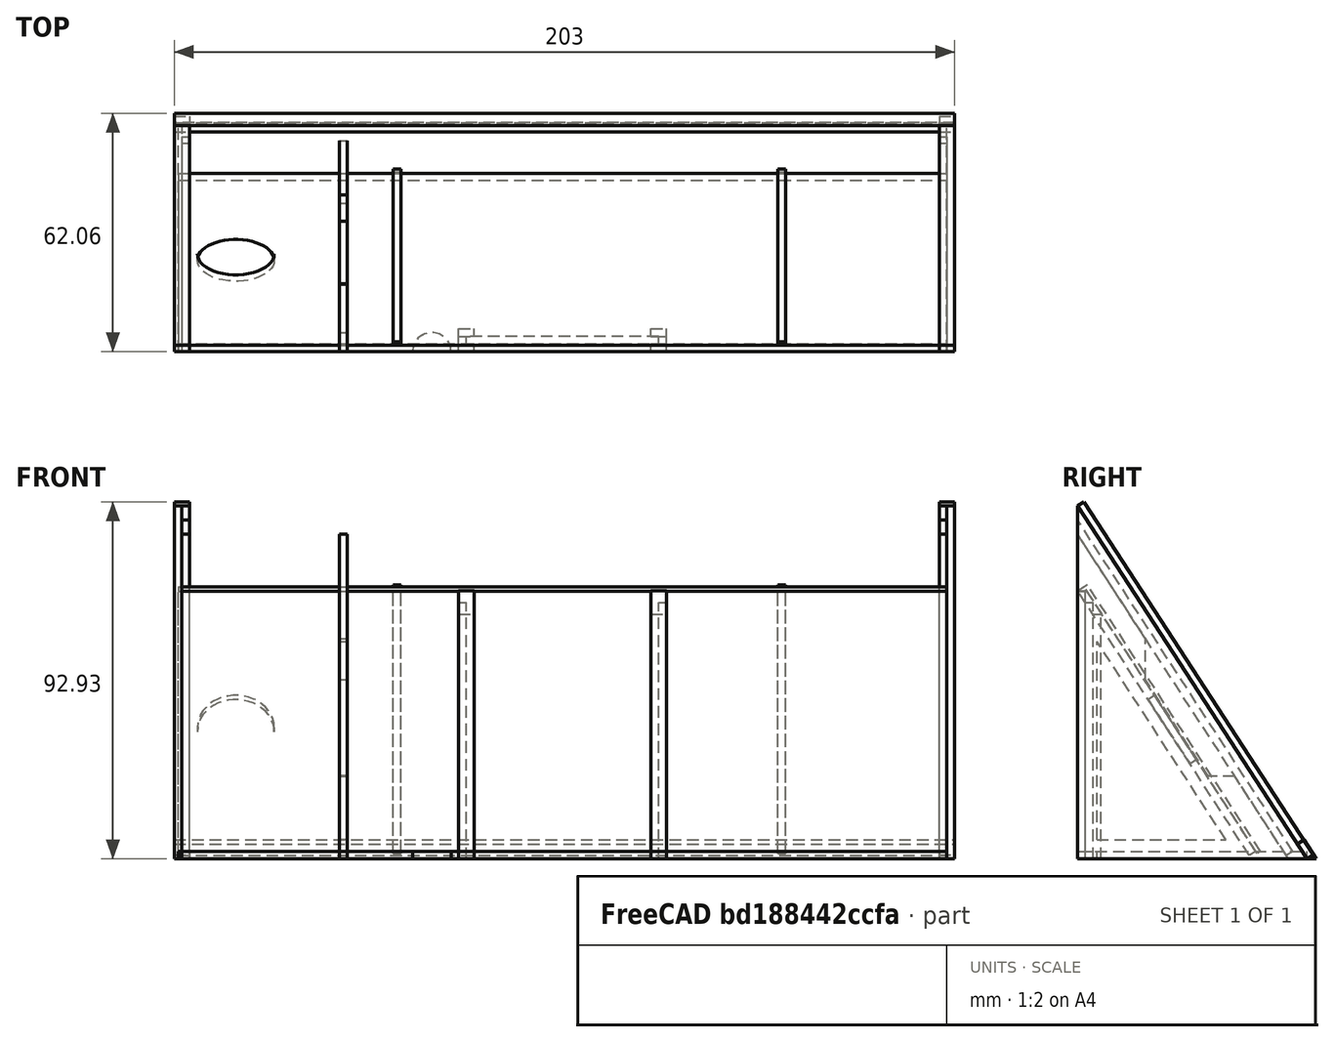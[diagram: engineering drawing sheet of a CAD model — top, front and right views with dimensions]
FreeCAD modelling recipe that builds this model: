
FCSTD DOCUMENT  (FreeCAD 0.16R)
Label: Phone_Stand_Version_1
License: All rights reserved
LicenseURL: http://en.wikipedia.org/wiki/All_rights_reserved
objects: Part::Box×37, Part::Cut×18, Part::Fuse×2, Part::Cylinder×2
note: 59 computed .brp shape members not serialized (recipe doc carries the construction recipe); baked Part::Feature solids carry a one-line shape summary decoded from their .brp

FEATURE [Part::Box] Box  label="Auflage"
  Height = 2
  Length = 200
  Placement = pos=(0,0,0) rot=(1,0,0;2.14676rad)
  Width = 82
FEATURE [Part::Box] Box001  label="Boden"
  Height = 2
  Length = 200
  Placement = pos=(0,-46.35,-2) rot=(0,0,1;0rad)
  Width = 59.65
FEATURE [Part::Box] Box002  label="Rückwand"
  Height = 67.682
  Length = 200
  Placement = pos=(0,-46.338,0) rot=(0,0,1;0rad)
  Width = 2
FEATURE [Part::Box] Box009  label="Cube008"
  Height = 50
  Length = 2
  Placement = pos=(0,13.3,-2) rot=(1,0,0;2.14676rad)
  Width = 110
FEATURE [Part::Box] Box010  label="Cube009"
  Height = 100
  Length = 2
  Placement = pos=(0,-96.35,-3) rot=(0,0,1;0rad)
  Width = 50
FEATURE [Part::Box] Box011  label="Cube010"
  Height = 30
  Length = 10
  Placement = pos=(0,-50,-32) rot=(0,0,1;0rad)
  Width = 70
FEATURE [Part::Cut] Cut002
  Base = -> Box009
  Tool = -> Box011
FEATURE [Part::Cut] Cut003  label="Seitenwand rechts"
  Base = -> Cut002
  Placement = pos=(-1,0,0) rot=(0,0,1;0rad)
  Tool = -> Box010
FEATURE [Part::Box] Box012  label="Cube011"
  Height = 50
  Length = 2
  Placement = pos=(0,13.3,-2) rot=(1,0,0;2.14676rad)
  Width = 110
FEATURE [Part::Box] Box013  label="Cube012"
  Height = 100
  Length = 2
  Placement = pos=(0,-96.35,-3) rot=(0,0,1;0rad)
  Width = 50
FEATURE [Part::Box] Box014  label="Cube013"
  Height = 30
  Length = 10
  Placement = pos=(0,-50,-32) rot=(0,0,1;0rad)
  Width = 70
FEATURE [Part::Cut] Cut004
  Base = -> Box012
  Tool = -> Box014
FEATURE [Part::Cut] Cut005  label="Seitenwand links"
  Base = -> Cut004
  Placement = pos=(200,0,0) rot=(0,0,1;0rad)
  Tool = -> Box013
FEATURE [Part::Box] Box016  label="Cube015"
  Height = 2
  Length = 2
  Placement = pos=(0,9.6,0) rot=(1,0,0;2.14676rad)
  Width = 110
FEATURE [Part::Box] Box017  label="Cube016"
  Height = 20
  Length = 10
  Placement = pos=(0,-56.35,80) rot=(0,0,1;0rad)
  Width = 10
FEATURE [Part::Cut] Cut  label="Führungsleiste links"
  Base = -> Box016
  Placement = pos=(198,0,0) rot=(0,0,1;0rad)
  Tool = -> Box017
FEATURE [Part::Box] Box019  label="Cube018"
  Height = 100
  Length = 2
  Placement = pos=(0,-96.35,-3) rot=(0,0,1;0rad)
  Width = 50
FEATURE [Part::Box] Box028  label="Cube026"
  Height = 15
  Length = 2
  Placement = pos=(-40,13.3,-2) rot=(1,0,0;2.14676rad)
  Width = 110
FEATURE [Part::Box] Box029  label="Cube027"
  Height = 10
  Length = 2
  Placement = pos=(-40,-4,25) rot=(1,0,0;2.14676rad)
  Width = 30
FEATURE [Part::Box] Box030  label="Cube028"
  Height = 70
  Length = 2
  Placement = pos=(-40,-46.35,-2) rot=(0,0,1;0rad)
  Width = 5
FEATURE [Part::Box] Box031  label="Cube029"
  Height = 5
  Length = 2
  Placement = pos=(-40,-46.35,-2) rot=(0,0,1;0rad)
  Width = 50
FEATURE [Part::Box] Box032  label="Cube030"
  Height = 95
  Length = 2
  Placement = pos=(-40,-61.35,-2) rot=(0,0,1;0rad)
  Width = 15
FEATURE [Part::Box] Box033  label="Cube031"
  Height = 10
  Length = 2
  Placement = pos=(-40,-46.35,-12) rot=(0,0,1;0rad)
  Width = 65
FEATURE [Part::Cut] Cut013
  Base = -> Box028
  Tool = -> Box032
FEATURE [Part::Cut] Cut014
  Base = -> Cut013
  Tool = -> Box033
FEATURE [Part::Cut] Cut015  label="Seitenwand rechts001"
  Base = -> Cut003
  Tool = -> Box019
FEATURE [Part::Cut] Cut016
  Base = -> Cut014
  Tool = -> Box029
FEATURE [Part::Fuse] Fusion
  Base = -> Cut016
  Tool = -> Box030
FEATURE [Part::Fuse] Fusion001  label="Innenwand"
  Base = -> Fusion
  Tool = -> Box031
FEATURE [Part::Box] Box035  label="Abdeckung rechts"
  Height = 2
  Length = 4
  Placement = pos=(-1,14.95,-0.9) rot=(1,0,0;2.14676rad)
  Width = 109.5
FEATURE [Part::Box] Box036  label="Abdeckung unten 001"
  Height = 2
  Length = 203
  Placement = pos=(-1,15.75,-2.1) rot=(1,0,0;2.14676rad)
  Width = 6
FEATURE [Part::Box] Box037  label="Cube034"
  Height = 2
  Length = 2
  Placement = pos=(1,9.6,0) rot=(1,0,0;2.14676rad)
  Width = 110
FEATURE [Part::Box] Box039  label="Cube036"
  Height = 5
  Length = 2
  Placement = pos=(-40,19.65,-10) rot=(1,0,0;2.14676rad)
  Width = 120
FEATURE [Part::Cut] Cut017  label="Innenwand001"
  Base = -> Fusion001
  Placement = pos=(82,0,0) rot=(0,0,1;0rad)
  Tool = -> Box039
FEATURE [Part::Box] Box040  label="Führungsleiste mitte links"
  Height = 1
  Length = 2
  Placement = pos=(156,1.2,0) rot=(1,0,0;2.14676rad)
  Width = 82.65
FEATURE [Part::Box] Box041  label="Führungsleiste mitte rechts"
  Height = 1
  Length = 2
  Placement = pos=(56,1.2,0) rot=(1,0,0;2.14676rad)
  Width = 82.65
FEATURE [Part::Cylinder] Cylinder
  Angle = 360
  Height = 10
  Placement = pos=(15,-15,36) rot=(1,0,0;2.14676rad)
  Radius = 10
FEATURE [Part::Cut] Cut018  label="Auflage001"
  Base = -> Box
  Tool = -> Cylinder
FEATURE [Part::Box] Box043  label="Cube038"
  Height = 10
  Length = 50
  Placement = pos=(75,-44.35,-5) rot=(0,0,1;0rad)
  Width = 2
FEATURE [Part::Box] Box045  label="Cube040"
  Height = 63.7
  Length = 4
  Placement = pos=(73,-42.35,-2) rot=(0,0,1;0rad)
  Width = 2
FEATURE [Part::Box] Box046  label="Cube041"
  Height = 66.7
  Length = 2
  Placement = pos=(73,-44.35,-2) rot=(0,0,1;0rad)
  Width = 2
FEATURE [Part::Box] Box047  label="Cube042"
  Height = 69.7
  Length = 4
  Placement = pos=(73,-46.35,-2) rot=(0,0,1;0rad)
  Width = 2
FEATURE [Part::Box] Box048  label="Cube043"
  Height = 63.7
  Length = 4
  Placement = pos=(123,-42.35,-2) rot=(0,0,1;0rad)
  Width = 2
FEATURE [Part::Box] Box049  label="Cube044"
  Height = 66.7
  Length = 2
  Placement = pos=(125,-44.35,-2) rot=(0,0,1;0rad)
  Width = 2
FEATURE [Part::Box] Box050  label="Cube045"
  Height = 69.7
  Length = 4
  Placement = pos=(123,-46.35,-2) rot=(0,0,1;0rad)
  Width = 2
FEATURE [Part::Box] Box051  label="Cube046"
  Height = 10
  Length = 46
  Placement = pos=(77,-46.35,-5) rot=(0,0,1;0rad)
  Width = 2
FEATURE [Part::Cut] Cut019
  Base = -> Box001
  Tool = -> Box043
FEATURE [Part::Cut] Cut020  label="Boden001"
  Base = -> Cut019
  Tool = -> Box051
FEATURE [Part::Cylinder] Cylinder001
  Angle = 360
  Height = 10
  Placement = pos=(66,-46.35,-5) rot=(0,0,1;0rad)
  Radius = 5
FEATURE [Part::Cut] Cut021  label="Boden002"
  Base = -> Cut020
  Tool = -> Cylinder001
FEATURE [Part::Box] Box053  label="Cube"
  Height = 20
  Length = 10
  Placement = pos=(-5,-56.35,80) rot=(0,0,1;0rad)
  Width = 10
FEATURE [Part::Cut] Cut022  label="Führungsleiste rechts"
  Base = -> Box037
  Tool = -> Box053
FEATURE [Part::Box] Box054  label="Abdeckung links"
  Height = 2
  Length = 4
  Placement = pos=(198,14.95,-0.9) rot=(1,0,0;2.14676rad)
  Width = 109.5
FEATURE [Part::Box] Box055  label="Cube047"
  Height = 10
  Length = 205
  Placement = pos=(-2,8,-12) rot=(0,0,1;0rad)
  Width = 10
FEATURE [Part::Cut] Cut023  label="Abdeckung unten"
  Base = -> Box036
  Tool = -> Box055
FEATURE [Part::Box] Box056  label="Cube048"
  Height = 10
  Length = 10
  Placement = pos=(40,-12.36,19.55) rot=(0,0,1;0rad)
  Width = 10
FEATURE [Part::Cut] Cut024
  Base = -> Cut017
  Tool = -> Box056
FEATURE [Part::Box] Box057  label="Cube049"
  Height = 15
  Length = 10
  Placement = pos=(40,-28.73,44.7) rot=(0,0,1;0rad)
  Width = 10
FEATURE [Part::Cut] Cut025  label="Zwischenwand"
  Base = -> Cut024
  Tool = -> Box057
